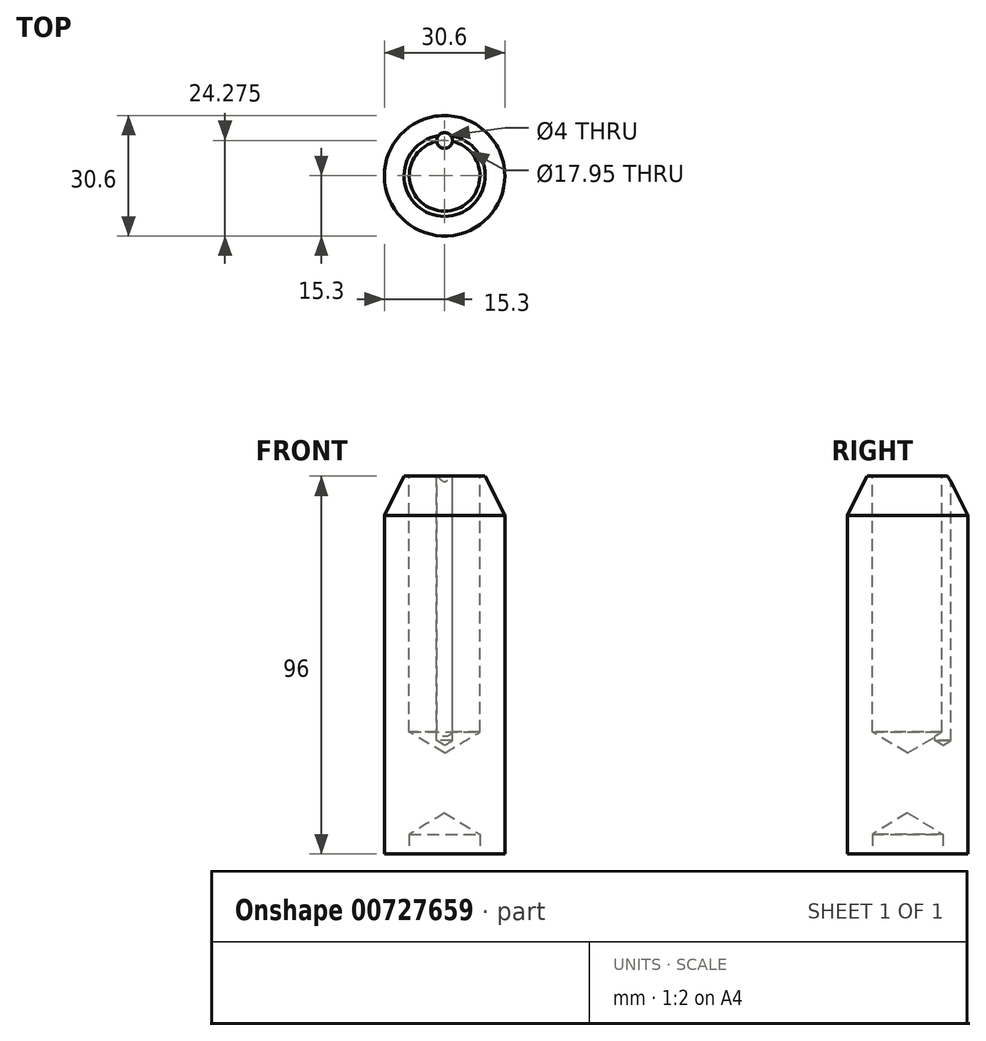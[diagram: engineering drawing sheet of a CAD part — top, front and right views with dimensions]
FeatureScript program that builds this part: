
annotation { "Feature Type Name" : "Feature", "Feature Type Description" : "" }
export const myFeature = defineFeature(function(context is Context, id is Id, definition is map)
    precondition{}
    {
        {
            var Q0;
            Q0=qCreatedBy(makeId("Top.planeOp"),FACE);
            var sketch = newSketch(context, id + "F0", { "sketchPlane" : qUnion([Q0])});
            skCircle(sketch, "E0", {"center": v(0, 0) * mm, "radius": 15.3 * mm});
            skSolve(sketch);
        }
        {
            var Q0;
            Q0=makeQuery(id+"F0.imprint","IMPRINT",FACE,{"disambiguationData":[TD([[makeQuery(id+"F0.imprint","IMPRINT",EDGE,{"derivedFrom":sQuery(id+"F0.wireOp",EDGE,"E0")}),1.0]])]});
            extrude(context, id + "F1", {"entities" : qUnion([Q0]), "depth" : 96 * mm, "offsetDistance" : 25 * mm});
        }
        {
            var Q0;
            Q0=makeQuery(id+"F1.opExtrude","CAP_FACE",FACE,{"disambiguationData":[OSD([sQuery(id+"F0.wireOp",EDGE,"E0")])],"isStart":false});
            var sketch = newSketch(context, id + "F2", { "sketchPlane" : qUnion([Q0])});
            skCircle(sketch, "E1", {"center": v(0, 0) * mm, "radius": 2.76 * mm});
            skSolve(sketch);
        }
        {
            var Q0;
            Q0=sQuery(id+"F2.wireOp",VERTEX,"E1.center");
            var Q1;
            Q1=makeQuery(id+"F1.opExtrude","SWEPT_BODY",BODY,{"disambiguationData":[OSD([sQuery(id+"F0.wireOp",EDGE,"E0")])]});
            hole(context, id + "F3", {"style" : HoleStyle.SIMPLE, "endStyle" : HoleEndStyle.BLIND, "holeDiameter" : 17.95 * mm, "majorDiameter" : 5 * mm, "holeDepth" : 65 * mm, "isTappedThrough" : true, "tappedDepth" : 12 * mm, "tapClearance" : 3, "startFromSketch" : true, "locations" : qUnion([Q0]), "scope" : qUnion([Q1])});
        }
        {
            var Q0;
            Q0=makeQuery(id+"F1.opExtrude","CAP_EDGE",EDGE,{"disambiguationData":[OSD([sQuery(id+"F0.wireOp",EDGE,"E0")])],"isStart":false});
            chamfer(context, id + "F4", {"entities" : qUnion([Q0]), "chamferType" : ChamferType.TWO_OFFSETS, "width1" : 5 * mm, "oppositeDirection" : false, "width2" : 10 * mm, "tangentPropagation" : true});
        }
        {
            var Q0;
            Q0=makeQuery(id+"F1.opExtrude","CAP_FACE",FACE,{"disambiguationData":[OSD([sQuery(id+"F0.wireOp",EDGE,"E0")])],"isStart":false});
            var sketch = newSketch(context, id + "F5", { "sketchPlane" : qUnion([Q0])});
            skCircle(sketch, "E2", {"center": v(0, 8.97) * mm, "radius": 0.72 * mm});
            skCircle(sketch, "E3", {"center": v(0, -8.97) * mm, "radius": 0.83 * mm});
            skSolve(sketch);
        }
        {
            var Q0;
            Q0=sQuery(id+"F5.wireOp",VERTEX,"E2.center");
            var Q1;
            Q1=makeQuery(id+"F1.opExtrude","SWEPT_BODY",BODY,{"disambiguationData":[OSD([sQuery(id+"F0.wireOp",EDGE,"E0")])]});
            hole(context, id + "F6", {"style" : HoleStyle.SIMPLE, "endStyle" : HoleEndStyle.BLIND, "holeDiameter" : 4 * mm, "majorDiameter" : 5 * mm, "holeDepth" : 1 * mm, "isTappedThrough" : true, "tappedDepth" : 12 * mm, "tapClearance" : 3, "locations" : qUnion([Q0]), "scope" : qUnion([Q1])});
        }
        {
            var Q0;
            Q0=qCreatedBy(makeId("Top.planeOp"),FACE);
            var sketch = newSketch(context, id + "F7", { "sketchPlane" : qUnion([Q0])});
            skCircle(sketch, "E4", {"center": v(0, 0) * mm, "radius": 3.56 * mm});
            skSolve(sketch);
        }
        {
            var Q0;
            Q0=sQuery(id+"F7.wireOp",VERTEX,"E4.center");
            var Q1;
            Q1=makeQuery(id+"F1.opExtrude","SWEPT_BODY",BODY,{"disambiguationData":[OSD([sQuery(id+"F0.wireOp",EDGE,"E0")])]});
            hole(context, id + "F8", {"style" : HoleStyle.SIMPLE, "endStyle" : HoleEndStyle.BLIND, "oppositeDirection" : true, "holeDiameter" : 17.95 * mm, "majorDiameter" : 5 * mm, "holeDepth" : 5 * mm, "isTappedThrough" : true, "tappedDepth" : 12 * mm, "tapClearance" : 3, "startFromSketch" : true, "locations" : qUnion([Q0]), "scope" : qUnion([Q1])});
        }
    });
